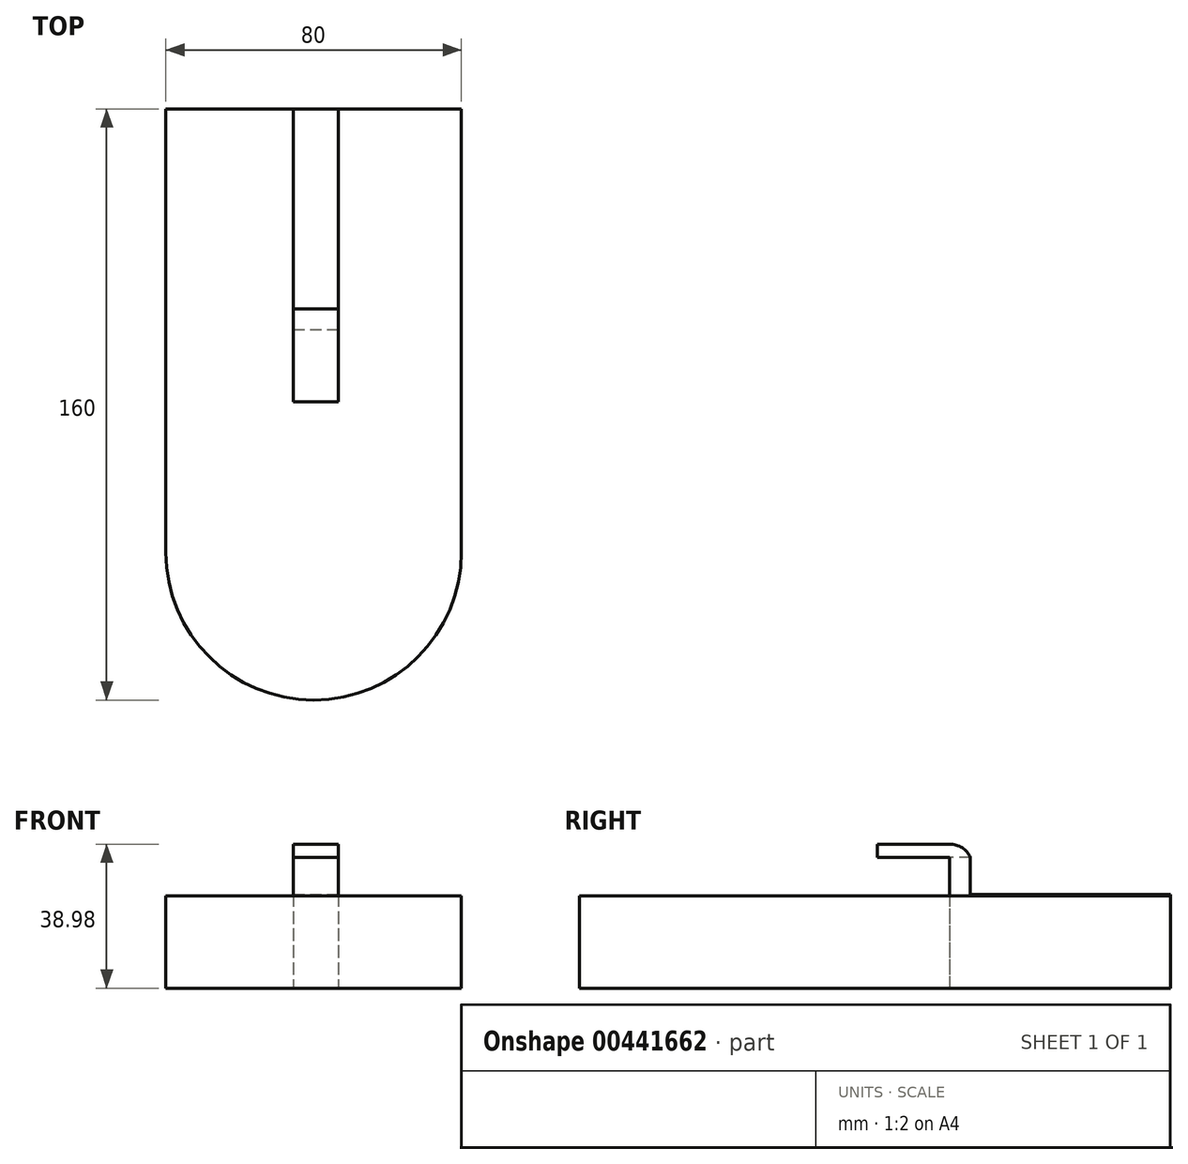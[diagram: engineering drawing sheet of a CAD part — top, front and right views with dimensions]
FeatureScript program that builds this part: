
annotation { "Feature Type Name" : "Feature", "Feature Type Description" : "" }
export const myFeature = defineFeature(function(context is Context, id is Id, definition is map)
    precondition{}
    {
        {
            var Q0;
            Q0=qCreatedBy(makeId("Top.planeOp"),FACE);
            var sketch = newSketch(context, id + "F0", { "sketchPlane" : qUnion([Q0])});
            skLineSegment(sketch, "E0.bottom", {"start": v(-40.6, 58.96) * mm, "end": v(39.4, 58.96) * mm});
            skLineSegment(sketch, "E0.top", {"start": v(-40.6, -61.04) * mm, "end": v(39.4, -61.04) * mm});
            skLineSegment(sketch, "E0.left", {"start": v(-40.6, 58.96) * mm, "end": v(-40.6, -61.04) * mm});
            skLineSegment(sketch, "E0.right", {"start": v(39.4, 58.96) * mm, "end": v(39.4, -61.04) * mm});
            skLineSegment(sketch, "E1.bottom", {"start": v(-6.08, 58.96) * mm, "end": v(6.08, 58.96) * mm});
            skLineSegment(sketch, "E1.top", {"start": v(-6.08, -0.8) * mm, "end": v(6.08, -0.8) * mm});
            skLineSegment(sketch, "E1.left", {"start": v(-6.08, 58.96) * mm, "end": v(-6.08, -0.8) * mm});
            skLineSegment(sketch, "E1.right", {"start": v(6.08, 58.96) * mm, "end": v(6.08, -0.8) * mm});
            skPoint(sketch, "E1.middle", {"position": v(0, 29.08) * mm});
            skLineSegment(sketch, "E2.top", {"start": v(-6.08, 76.04) * mm, "end": v(6.08, 76.04) * mm});
            skLineSegment(sketch, "E2.left", {"start": v(-6.08, 58.96) * mm, "end": v(-6.08, 76.04) * mm});
            skLineSegment(sketch, "E2.right", {"start": v(6.08, 58.96) * mm, "end": v(6.08, 76.04) * mm});
            skArc(sketch, "E3", {"start": v(-40.6, -61.04) * mm, "mid": v(-0.6, -101.04) * mm, "end": v(39.4, -61.04) * mm});
            skSolve(sketch);
        }
        {
            var Q0;
            Q0=makeQuery(id+"F0.imprint","IMPRINT",FACE,{"disambiguationData":[TD([[makeQuery(id+"F0.imprint","IMPRINT",EDGE,{"derivedFrom":sQuery(id+"F0.wireOp",EDGE,"E0.top")}),1.0]])]});
            var Q1;
            Q1=makeQuery(id+"F0.imprint","IMPRINT",FACE,{"disambiguationData":[TD([[makeQuery(id+"F0.imprint","IMPRINT",EDGE,{"derivedFrom":sQuery(id+"F0.wireOp",EDGE,"E0.top")}),-1.0]])]});
            extrude(context, id + "F1", {"entities" : qUnion([Q0, Q1]), "depth" : 25 * mm});
        }
        {
            var Q0;
            Q0=makeQuery(id+"F0.imprint","IMPRINT",FACE,{"disambiguationData":[TD([[makeQuery(id+"F0.imprint","IMPRINT",EDGE,{"derivedFrom":sQuery(id+"F0.wireOp",EDGE,"E1.top")}),1.0]])]});
            var Q1;
            Q1=makeQuery(id+"F0.imprint","IMPRINT",FACE,{"disambiguationData":[TD([[makeQuery(id+"F0.imprint","IMPRINT",EDGE,{"derivedFrom":sQuery(id+"F0.wireOp",EDGE,"E1.bottom")}),1.0]])]});
            extrude(context, id + "F2", {"entities" : qUnion([Q0, Q1]), "depth" : 25.4 * mm});
        }
        {
            var Q0;
            Q0=makeQuery(id+"F2.opExtrude","CAP_FACE",FACE,{"disambiguationData":[OSD([sQuery(id+"F0.wireOp",EDGE,"E1.top"),sQuery(id+"F0.wireOp",EDGE,"E1.left"),sQuery(id+"F0.wireOp",EDGE,"E1.right"),sQuery(id+"F0.wireOp",EDGE,"E2.top"),sQuery(id+"F0.wireOp",EDGE,"E2.left"),sQuery(id+"F0.wireOp",EDGE,"E2.right")])],"isStart":false});
            var sketch = newSketch(context, id + "F3", { "sketchPlane" : qUnion([Q0])});
            skLineSegment(sketch, "E4.bottom", {"start": v(-6.08, -0.8) * mm, "end": v(6.08, -0.8) * mm});
            skLineSegment(sketch, "E4.top", {"start": v(-6.08, 4.76) * mm, "end": v(6.08, 4.76) * mm});
            skLineSegment(sketch, "E4.left", {"start": v(-6.08, -0.8) * mm, "end": v(-6.08, 4.76) * mm});
            skLineSegment(sketch, "E4.right", {"start": v(6.08, -0.8) * mm, "end": v(6.08, 4.76) * mm});
            skLineSegment(sketch, "E5.bottom", {"start": v(6.08, -0.8) * mm, "end": v(-6.08, -0.8) * mm});
            skLineSegment(sketch, "E5.top", {"start": v(6.08, -0.8) * mm, "end": v(-6.08, -0.8) * mm});
            skLineSegment(sketch, "E5.left", {"start": v(6.08, -0.8) * mm, "end": v(6.08, -0.8) * mm});
            skLineSegment(sketch, "E5.right", {"start": v(-6.08, -0.8) * mm, "end": v(-6.08, -0.8) * mm});
            skSolve(sketch);
        }
        {
            var Q0;
            Q0=makeQuery(id+"F3.imprint","IMPRINT",FACE,{"disambiguationData":[TD([[makeQuery(id+"F3.imprint","IMPRINT",EDGE,{"derivedFrom":sQuery(id+"F3.wireOp",EDGE,"E4.top")}),-1.0]])]});
            extrude(context, id + "F4", {"entities" : qUnion([Q0]), "operationType" : NewBodyOperationType.ADD, "depth" : 10 * mm});
        }
        {
            var Q0;
            Q0=makeQuery(id+"F4.boolean.opBoolean","MERGE",FACE,{"derivedFrom":[makeQuery(id+"F2.opExtrude","SWEPT_FACE",FACE,{"disambiguationData":[OSD([sQuery(id+"F0.wireOp",EDGE,"E1.right"),sQuery(id+"F0.wireOp",EDGE,"E2.right")])]}),makeQuery(id+"F4.opExtrude","SWEPT_FACE",FACE,{"disambiguationData":[OSD([sQuery(id+"F3.wireOp",EDGE,"E4.right")])]})]});
            var sketch = newSketch(context, id + "F5", { "sketchPlane" : qUnion([Q0])});
            skLineSegment(sketch, "E6.bottom", {"start": v(-0.8, 35.4) * mm, "end": v(-20.38, 35.4) * mm});
            skLineSegment(sketch, "E6.top", {"start": v(-0.8, 38.98) * mm, "end": v(-20.38, 38.98) * mm});
            skLineSegment(sketch, "E6.left", {"start": v(-0.8, 35.4) * mm, "end": v(-0.8, 38.98) * mm});
            skLineSegment(sketch, "E6.right", {"start": v(-20.38, 35.4) * mm, "end": v(-20.38, 38.98) * mm});
            skArc(sketch, "E7", {"start": v(4.76, 35.4) * mm, "mid": v(2.5, 38) * mm, "end": v(-0.8, 38.98) * mm});
            skSolve(sketch);
        }
        {
            var Q0;
            Q0=makeQuery(id+"F5.imprint","IMPRINT",FACE,{"disambiguationData":[TD([[makeQuery(id+"F5.imprint","IMPRINT",EDGE,{"derivedFrom":sQuery(id+"F5.wireOp",EDGE,"E6.left")}),-1.0]])]});
            var Q1;
            Q1=makeQuery(id+"F5.imprint","IMPRINT",FACE,{"disambiguationData":[TD([[makeQuery(id+"F5.imprint","IMPRINT",EDGE,{"derivedFrom":sQuery(id+"F5.wireOp",EDGE,"E6.bottom")}),-1.0]])]});
            extrude(context, id + "F6", {"entities" : qUnion([Q0, Q1]), "operationType" : NewBodyOperationType.ADD, "depth" : -12.2 * mm});
        }
    });
